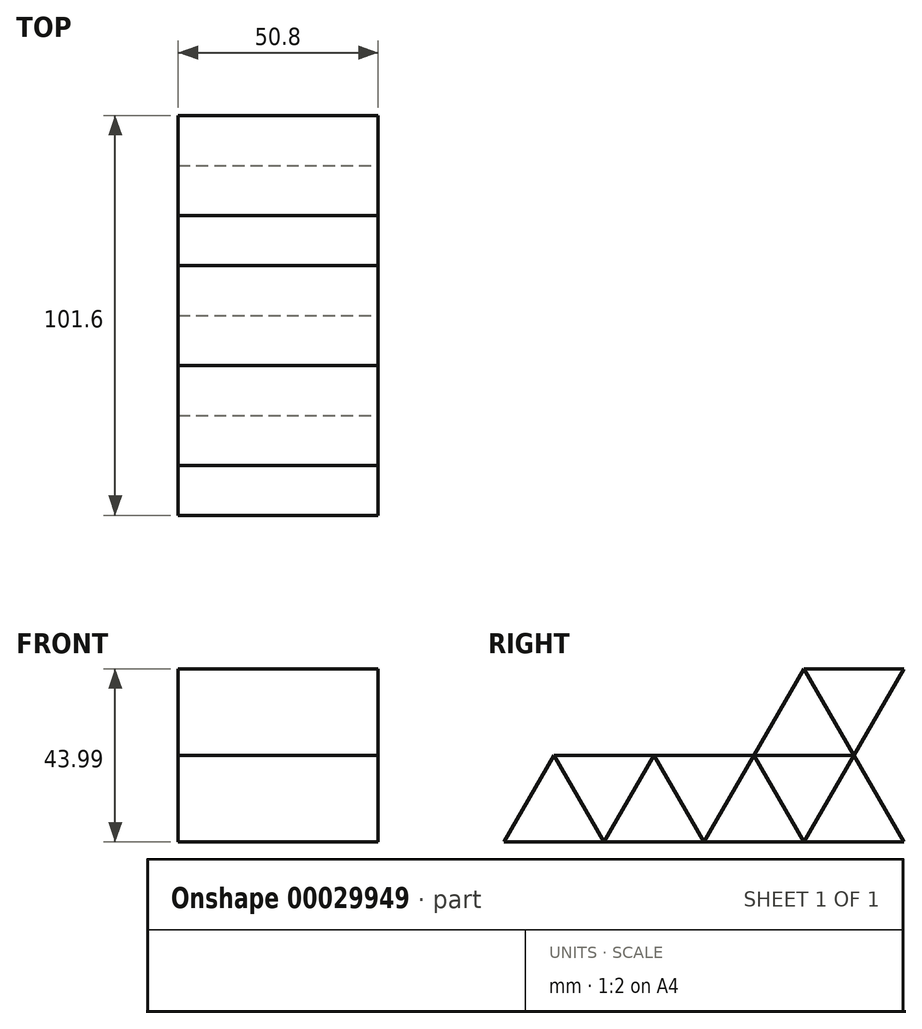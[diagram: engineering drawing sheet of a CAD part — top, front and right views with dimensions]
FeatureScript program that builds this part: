
annotation { "Feature Type Name" : "Feature", "Feature Type Description" : "" }
export const myFeature = defineFeature(function(context is Context, id is Id, definition is map)
    precondition{}
    {
        {
            var Q0;
            Q0=qCreatedBy(makeId("Right.planeOp"),FACE);
            var sketch = newSketch(context, id + "F0", { "sketchPlane" : qUnion([Q0])});
            skLineSegment(sketch, "E0", {"start": v(0, 0) * mm, "end": v(-12.7, 22) * mm});
            skLineSegment(sketch, "E1", {"start": v(-12.7, 22) * mm, "end": v(-25.4, 0) * mm});
            skLineSegment(sketch, "E2", {"start": v(0, 0) * mm, "end": v(-25.4, 0) * mm});
            skLineSegment(sketch, "E3.1.0.0", {"start": v(-25.4, 0) * mm, "end": v(-50.8, 0) * mm});
            skLineSegment(sketch, "E3.1.0.1", {"start": v(-25.4, 0) * mm, "end": v(-38.1, 22) * mm});
            skLineSegment(sketch, "E3.1.0.2", {"start": v(-38.1, 22) * mm, "end": v(-50.8, 0) * mm});
            skLineSegment(sketch, "E3.2.0.0", {"start": v(-50.8, 0) * mm, "end": v(-76.2, 0) * mm});
            skLineSegment(sketch, "E3.2.0.1", {"start": v(-50.8, 0) * mm, "end": v(-63.5, 22) * mm});
            skLineSegment(sketch, "E3.2.0.2", {"start": v(-63.5, 22) * mm, "end": v(-76.2, 0) * mm});
            skLineSegment(sketch, "E3.3.0.0", {"start": v(-76.2, 0) * mm, "end": v(-101.6, 0) * mm});
            skLineSegment(sketch, "E3.3.0.1", {"start": v(-76.2, 0) * mm, "end": v(-88.9, 22) * mm});
            skLineSegment(sketch, "E3.3.0.2", {"start": v(-88.9, 22) * mm, "end": v(-101.6, 0) * mm});
            skLineSegment(sketch, "E3.direction1", {"start": v(-25.4, 0) * mm, "end": v(-50.8, 0) * mm, "construction": true});
            skLineSegment(sketch, "E4", {"start": v(-88.9, 22) * mm, "end": v(-12.7, 22) * mm});
            skLineSegment(sketch, "E5.MirrorCS", {"start": v(0, 44) * mm, "end": v(-25.4, 44) * mm});
            skLineSegment(sketch, "E6.MirrorCS", {"start": v(0, 44) * mm, "end": v(-12.7, 22) * mm});
            skLineSegment(sketch, "E7.MirrorCS", {"start": v(-25.4, 44) * mm, "end": v(-38.1, 22) * mm});
            skLineSegment(sketch, "E8.MirrorCS", {"start": v(-12.7, 22) * mm, "end": v(-25.4, 44) * mm});
            skSolve(sketch);
        }
        {
            var Q0;
            Q0 = qSketchRegion(id + "F0", true);
            var Q1;
            Q1=sQuery(id+"F0.wireOp",EDGE,"E3.3.0.0");
            var Q2;
            Q2=sQuery(id+"F0.wireOp",EDGE,"E3.2.0.0");
            var Q3;
            Q3=sQuery(id+"F0.wireOp",EDGE,"E3.1.0.0");
            var Q4;
            Q4=sQuery(id+"F0.wireOp",EDGE,"E2");
            var Q5;
            Q5=sQuery(id+"F0.wireOp",EDGE,"E4");
            var Q6;
            Q6=sQuery(id+"F0.wireOp",EDGE,"E6.MirrorCS");
            var Q7;
            Q7=sQuery(id+"F0.wireOp",EDGE,"E5.MirrorCS");
            var Q8;
            Q8=sQuery(id+"F0.wireOp",EDGE,"E3.3.0.2");
            extrude(context, id + "F1", {"entities" : qUnion([Q0]), "bodyType" : ToolBodyType.SURFACE, "surfaceEntities" : qUnion([Q1, Q2, Q3, Q4, Q5, Q6, Q7, Q8]), "depth" : 50.8 * mm});
        }
        {
            var Q0;
            Q0=qCreatedBy(makeId("Right.planeOp"),FACE);
            var sketch = newSketch(context, id + "F2", { "sketchPlane" : qUnion([Q0])});
            skLineSegment(sketch, "E9", {"start": v(0, 0) * mm, "end": v(-25.4, 44) * mm});
            skLineSegment(sketch, "E10", {"start": v(-25.4, 44) * mm, "end": v(-50.8, 0) * mm});
            skLineSegment(sketch, "E11", {"start": v(-50.8, 0) * mm, "end": v(-63.5, 22) * mm});
            skLineSegment(sketch, "E12", {"start": v(-63.5, 22) * mm, "end": v(-76.2, 0) * mm});
            skLineSegment(sketch, "E13", {"start": v(-76.2, 0) * mm, "end": v(-88.9, 22) * mm});
            skLineSegment(sketch, "E14", {"start": v(-38.1, 22) * mm, "end": v(-25.4, 0) * mm});
            skLineSegment(sketch, "E15", {"start": v(-25.4, 0) * mm, "end": v(-12.7, 22) * mm});
            skSolve(sketch);
        }
        {
            var Q0;
            Q0 = qSketchRegion(id + "F2", true);
            var Q1;
            Q1=sQuery(id+"F2.wireOp",EDGE,"E9");
            var Q2;
            Q2=sQuery(id+"F2.wireOp",EDGE,"E10");
            var Q3;
            Q3=sQuery(id+"F2.wireOp",EDGE,"E11");
            var Q4;
            Q4=sQuery(id+"F2.wireOp",EDGE,"E12");
            var Q5;
            Q5=sQuery(id+"F2.wireOp",EDGE,"E13");
            extrude(context, id + "F3", {"entities" : qUnion([Q0]), "bodyType" : ToolBodyType.SURFACE, "surfaceEntities" : qUnion([Q1, Q2, Q3, Q4, Q5]), "depth" : 50.8 * mm});
        }
        {
            var Q0;
            Q0=qCreatedBy(makeId("Right.planeOp"),FACE);
            var sketch = newSketch(context, id + "F4", { "sketchPlane" : qUnion([Q0])});
            skLineSegment(sketch, "E16", {"start": v(-12.7, 22) * mm, "end": v(-25.4, 0) * mm});
            skLineSegment(sketch, "E17", {"start": v(-25.4, 0) * mm, "end": v(-38.1, 22) * mm});
            skSolve(sketch);
        }
        {
            var Q0;
            Q0=sQuery(id+"F4.wireOp",EDGE,"E17");
            var Q1;
            Q1=sQuery(id+"F4.wireOp",EDGE,"E16");
            extrude(context, id + "F5", {"bodyType" : ToolBodyType.SURFACE, "surfaceEntities" : qUnion([Q0, Q1]), "depth" : 50.8 * mm});
        }
    });
